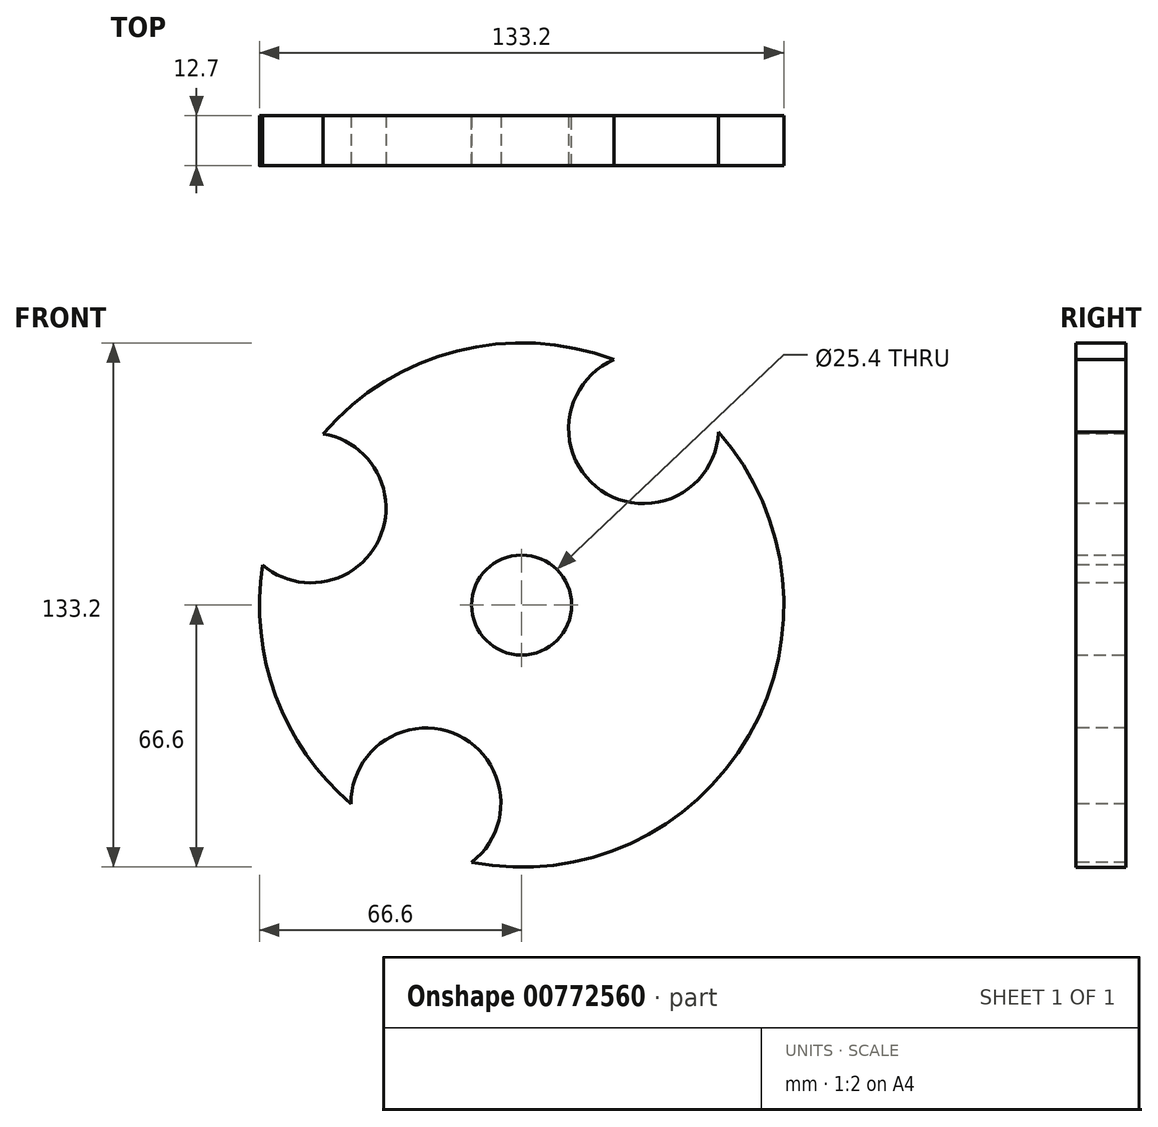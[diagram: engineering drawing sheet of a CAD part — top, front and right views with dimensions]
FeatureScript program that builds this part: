
annotation { "Feature Type Name" : "Feature", "Feature Type Description" : "" }
export const myFeature = defineFeature(function(context is Context, id is Id, definition is map)
    precondition{}
    {
        {
            var Q0;
            Q0=qCreatedBy(makeId("Front.planeOp"),FACE);
            var sketch = newSketch(context, id + "F0", { "sketchPlane" : qUnion([Q0])});
            skCircle(sketch, "E0", {"center": v(0, 0) * mm, "radius": 66.6 * mm});
            skSolve(sketch);
        }
        {
            var Q0;
            Q0 = qSketchRegion(id + "F0", true);
            extrude(context, id + "F1", {"entities" : qUnion([Q0]), "depth" : 12.7 * mm, "offsetDistance" : 25.4 * mm});
        }
        {
            var Q0;
            Q0=makeQuery(id+"F1.opExtrude","CAP_FACE",FACE,{"disambiguationData":[OSD([sQuery(id+"F0.wireOp",EDGE,"E0")])],"isStart":false});
            var sketch = newSketch(context, id + "F2", { "sketchPlane" : qUnion([Q0])});
            skPoint(sketch, "E1", {"position": v(30.99, 44.8) * mm});
            skPoint(sketch, "E2", {"position": v(-53.51, 24.68) * mm});
            skPoint(sketch, "E3", {"position": v(-24.31, -50.3) * mm});
            skPoint(sketch, "E4", {"position": v(42.27, -33.94) * mm});
            skSolve(sketch);
        }
        {
            var Q0;
            Q0=sQuery(id+"F0.wireOp",VERTEX,"E0.center");
            var Q1;
            Q1=makeQuery(id+"F1.opExtrude","SWEPT_BODY",BODY,{"disambiguationData":[OSD([sQuery(id+"F0.wireOp",EDGE,"E0")])]});
            hole(context, id + "F3", {"style" : HoleStyle.SIMPLE, "endStyle" : HoleEndStyle.THROUGH, "oppositeDirection" : true, "holeDiameter" : 25.4 * mm, "majorDiameter" : 6.35 * mm, "isTappedThrough" : true, "tappedDepth" : 12.7 * mm, "tapClearance" : 3, "locations" : qUnion([Q0]), "scope" : qUnion([Q1])});
        }
        {
            var Q0;
            Q0=sQuery(id+"F2.wireOp",VERTEX,"E2");
            var Q1;
            Q1=sQuery(id+"F2.wireOp",VERTEX,"E1");
            var Q2;
            Q2=sQuery(id+"F2.wireOp",VERTEX,"E3");
            var Q3;
            Q3=makeQuery(id+"F1.opExtrude","SWEPT_BODY",BODY,{"disambiguationData":[OSD([sQuery(id+"F0.wireOp",EDGE,"E0")])]});
            hole(context, id + "F4", {"style" : HoleStyle.SIMPLE, "endStyle" : HoleEndStyle.THROUGH, "holeDiameter" : 38.1 * mm, "majorDiameter" : 6.35 * mm, "isTappedThrough" : true, "tappedDepth" : 12.7 * mm, "tapClearance" : 3, "locations" : qUnion([Q0, Q1, Q2]), "scope" : qUnion([Q3])});
        }
    });
